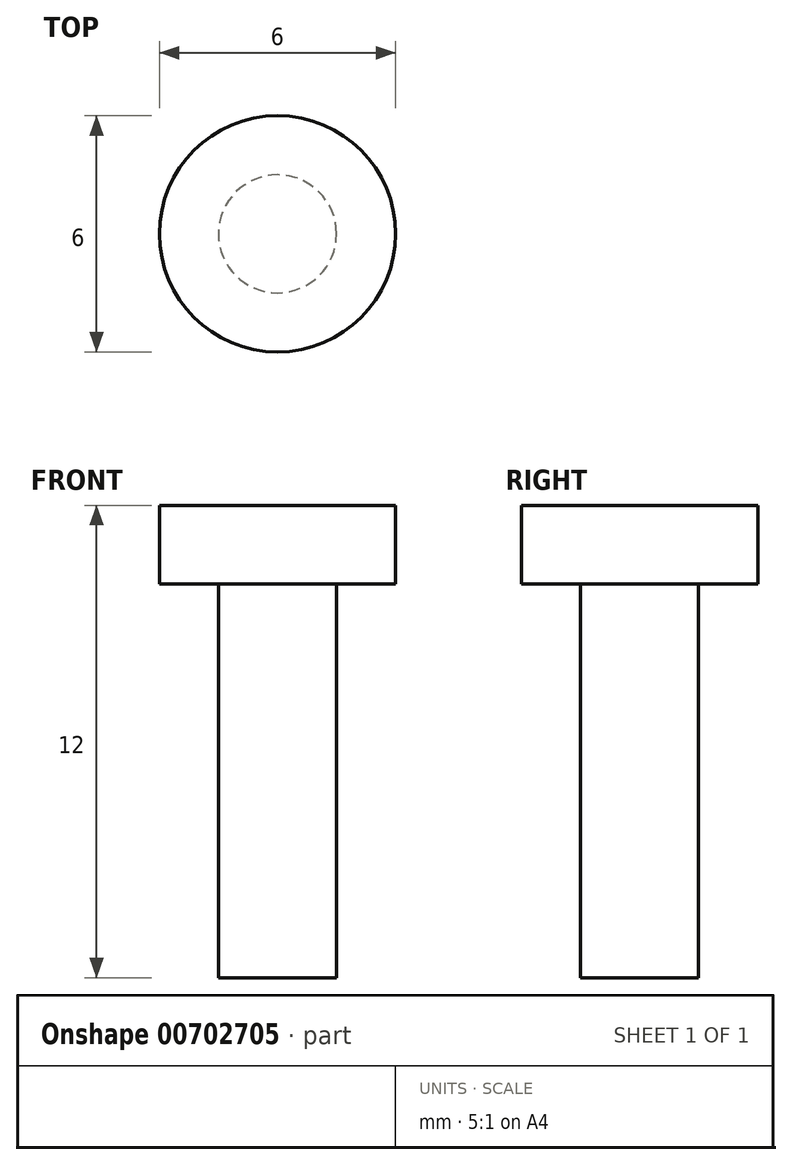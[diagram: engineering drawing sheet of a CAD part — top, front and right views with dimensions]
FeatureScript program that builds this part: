
annotation { "Feature Type Name" : "Feature", "Feature Type Description" : "" }
export const myFeature = defineFeature(function(context is Context, id is Id, definition is map)
    precondition{}
    {
        {
            var Q0;
            Q0=qCreatedBy(makeId("Front.planeOp"),FACE);
            var sketch = newSketch(context, id + "F0", { "sketchPlane" : qUnion([Q0])});
            skLineSegment(sketch, "E0", {"start": v(0, 12) * mm, "end": v(3, 12) * mm});
            skLineSegment(sketch, "E1", {"start": v(3, 12) * mm, "end": v(3, 10) * mm});
            skLineSegment(sketch, "E2", {"start": v(3, 10) * mm, "end": v(1.5, 10) * mm});
            skLineSegment(sketch, "E3", {"start": v(1.5, 10) * mm, "end": v(1.5, 0) * mm});
            skLineSegment(sketch, "E4", {"start": v(1.5, 0) * mm, "end": v(0, 0) * mm});
            skLineSegment(sketch, "E5", {"start": v(0, 0) * mm, "end": v(0, 12) * mm});
            skSolve(sketch);
        }
        {
            var Q0;
            Q0=makeQuery(id+"F0.imprint","IMPRINT",FACE,{"disambiguationData":[TD([[makeQuery(id+"F0.imprint","IMPRINT",EDGE,{"derivedFrom":sQuery(id+"F0.wireOp",EDGE,"E0")}),-1.0]])]});
            var Q1;
            Q1=sQuery(id+"F0.wireOp",EDGE,"E5");
            revolve(context, id + "F1", {"surfaceOperationType" : NewSurfaceOperationType.NEW, "entities" : qUnion([Q0]), "axis" : qUnion([Q1]), "revolveType" : RevolveType.FULL});
        }
    });
